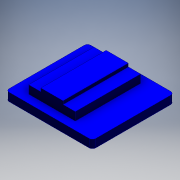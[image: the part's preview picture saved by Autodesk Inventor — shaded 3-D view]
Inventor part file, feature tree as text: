
AUTODESK INVENTOR PART (.ipt)
format: ipt  version: 2016 (Build 200138000, 138)  size: 166,400 bytes
history: native  units: mm
features: extrude x4, sketch x4
ambient origin geometry x8: Origin, YZ Plane, XZ Plane, XY Plane, X Axis, Y Axis, Z Axis, Center Point
bodies: Solid1 (feature_tree)
feature tree (8):
  extrude  "base"  Depth=53.0mm
  extrude  "magnetExt"  Depth=2.0mm
  extrude  "spacerOne"  Depth=50.0mm
  extrude  "sample"  Depth=2.0mm
  sketch  "Sketch1"  dims[d0=53.0mm d1=53.0mm]
  sketch  "Sketch3"  dims[d2=2.0mm d3=25.0mm]
  sketch  "Sketch7"  dims[d4=50.0mm d5=26.5mm]
  sketch  "Sketch8"  dims[d6=5.0mm d7=0.0mm d14=15.0mm d15=15.0mm d16=15.0mm d17=15.0mm d18=15.0mm d56=5.65mm d57=5.65mm d58=5.65mm d59=5.65mm d60=5.65mm d61=2.5mm d62=0.0mm d70=40.0mm d71=20.0mm d72=28.6mm d73=8.9mm d74=5.0mm d75=0.0mm d76=40.0mm d77=20.0mm d78=13.6mm d79=30.0mm d80=2.0mm d81=0.0mm]
